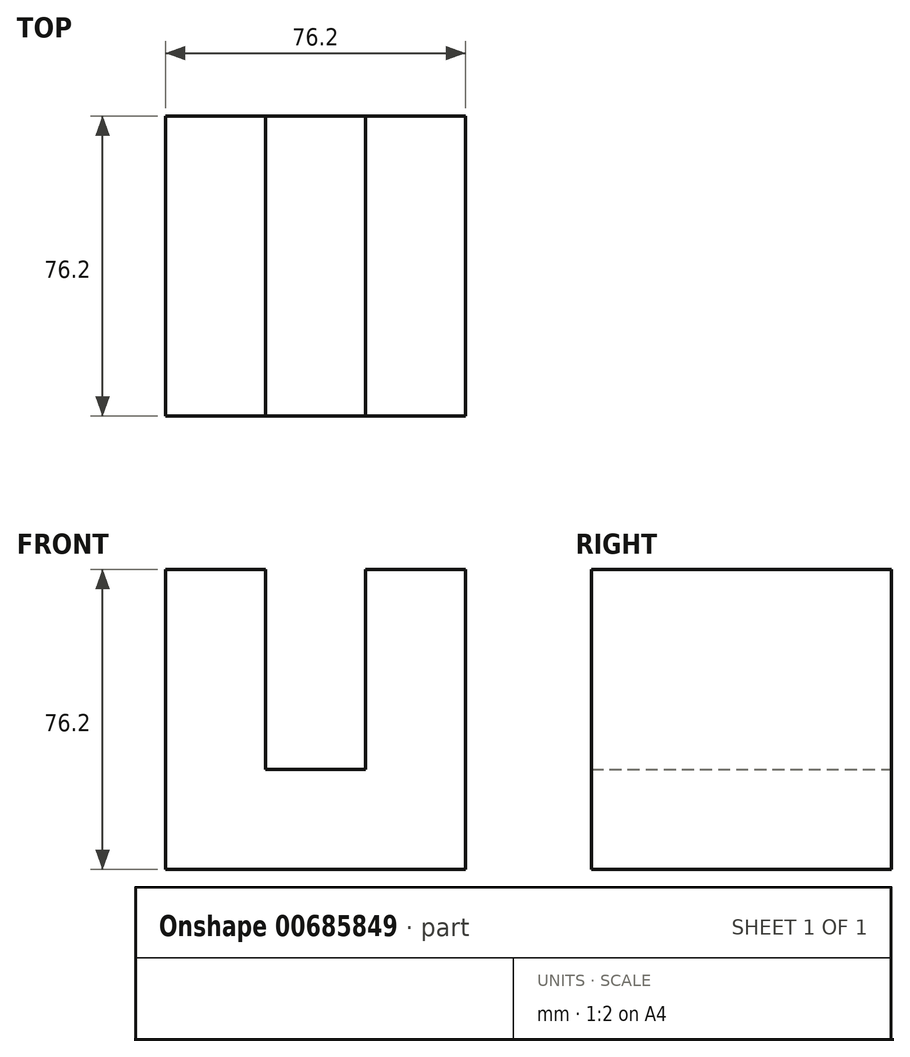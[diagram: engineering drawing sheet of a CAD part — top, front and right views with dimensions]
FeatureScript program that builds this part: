
annotation { "Feature Type Name" : "Feature", "Feature Type Description" : "" }
export const myFeature = defineFeature(function(context is Context, id is Id, definition is map)
    precondition{}
    {
        {
            var Q0;
            Q0=qCreatedBy(makeId("Front.planeOp"),FACE);
            var sketch = newSketch(context, id + "F0", { "sketchPlane" : qUnion([Q0])});
            skLineSegment(sketch, "E0", {"start": v(0, 0) * mm, "end": v(-76.2, 0) * mm});
            skLineSegment(sketch, "E1", {"start": v(-76.2, 0) * mm, "end": v(-76.2, 76.2) * mm});
            skLineSegment(sketch, "E2", {"start": v(-76.2, 76.2) * mm, "end": v(-50.8, 76.2) * mm});
            skLineSegment(sketch, "E3", {"start": v(-50.8, 76.2) * mm, "end": v(-50.8, 25.4) * mm});
            skLineSegment(sketch, "E4", {"start": v(0, 0) * mm, "end": v(0, 76.2) * mm});
            skLineSegment(sketch, "E5", {"start": v(0, 76.2) * mm, "end": v(-25.4, 76.2) * mm});
            skLineSegment(sketch, "E6", {"start": v(-25.4, 76.2) * mm, "end": v(-25.4, 25.4) * mm});
            skLineSegment(sketch, "E7", {"start": v(-50.8, 25.4) * mm, "end": v(-25.4, 25.4) * mm});
            skSolve(sketch);
        }
        {
            var Q0;
            Q0 = qSketchRegion(id + "F0", true);
            extrude(context, id + "F1", {"entities" : qUnion([Q0]), "depth" : 76.2 * mm, "offsetDistance" : 25.4 * mm});
        }
    });
